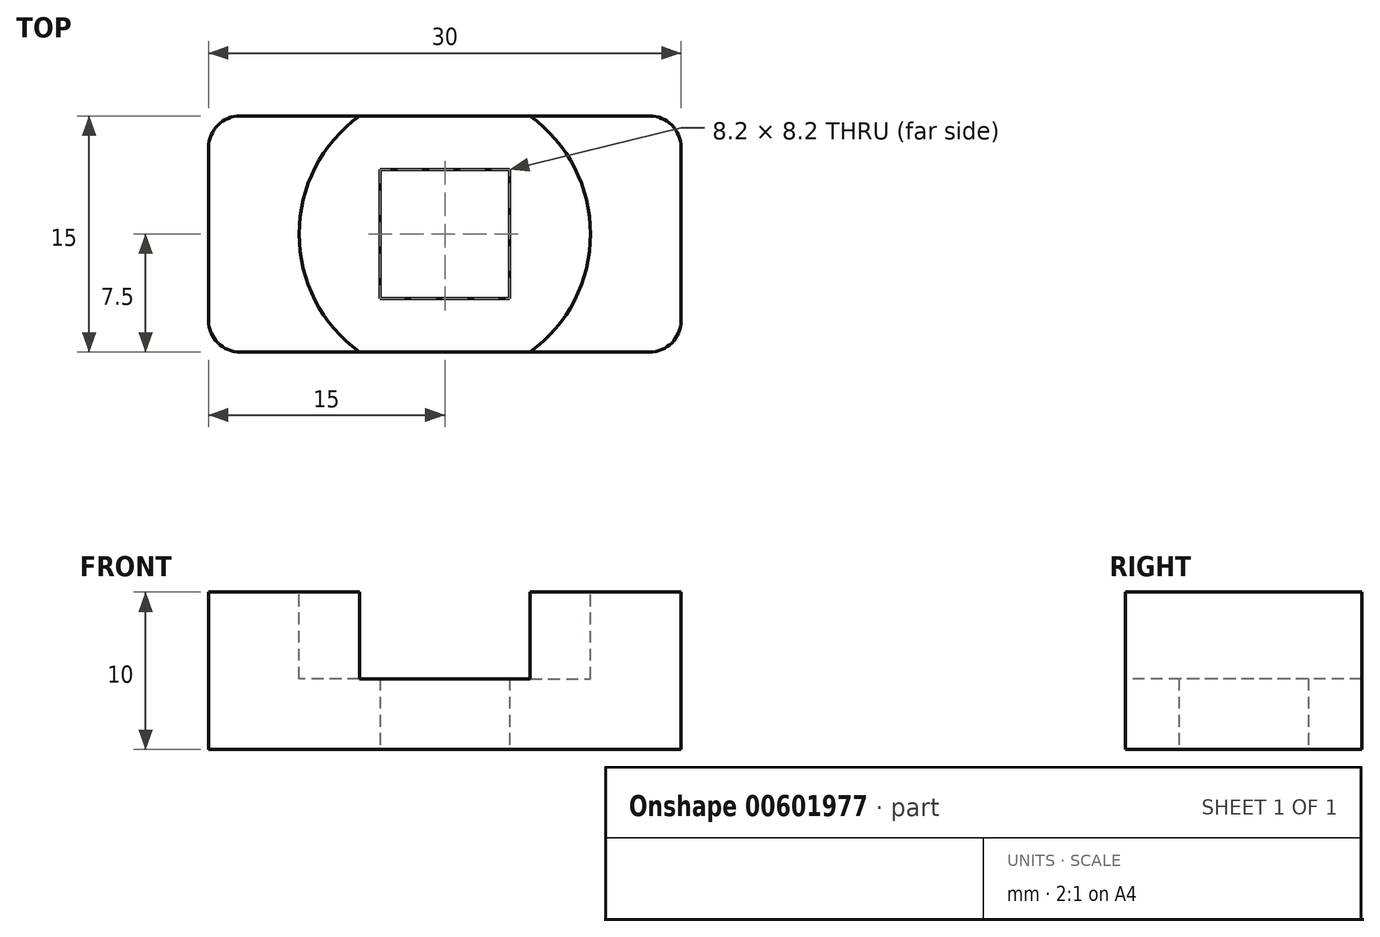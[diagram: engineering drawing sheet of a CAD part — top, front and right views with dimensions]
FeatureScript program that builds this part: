
annotation { "Feature Type Name" : "Feature", "Feature Type Description" : "" }
export const myFeature = defineFeature(function(context is Context, id is Id, definition is map)
    precondition{}
    {
        {
            var Q0;
            Q0=qCreatedBy(makeId("Top.planeOp"),FACE);
            var sketch = newSketch(context, id + "F0", { "sketchPlane" : qUnion([Q0])});
            skLineSegment(sketch, "E0.bottom", {"start": v(4.1, 4.1) * mm, "end": v(-4.1, 4.1) * mm});
            skLineSegment(sketch, "E0.top", {"start": v(4.1, -4.1) * mm, "end": v(-4.1, -4.1) * mm});
            skLineSegment(sketch, "E0.left", {"start": v(4.1, 4.1) * mm, "end": v(4.1, -4.1) * mm});
            skLineSegment(sketch, "E0.right", {"start": v(-4.1, 4.1) * mm, "end": v(-4.1, -4.1) * mm});
            skPoint(sketch, "E0.middle", {"position": v(0, 0) * mm});
            skLineSegment(sketch, "E1.bottom", {"start": v(13, 7.5) * mm, "end": v(-13, 7.5) * mm});
            skLineSegment(sketch, "E1.top", {"start": v(13, -7.5) * mm, "end": v(-13, -7.5) * mm});
            skLineSegment(sketch, "E1.left", {"start": v(15, 5.5) * mm, "end": v(15, -5.5) * mm});
            skLineSegment(sketch, "E1.right", {"start": v(-15, 5.5) * mm, "end": v(-15, -5.5) * mm});
            skPoint(sketch, "E2.visualSharp", {"position": v(15, 7.5) * mm});
            skArc(sketch, "E2.filletArc", {"start": v(15, 5.5) * mm, "mid": v(14.41, 6.91) * mm, "end": v(13, 7.5) * mm});
            skPoint(sketch, "E3.visualSharp", {"position": v(-15, 7.5) * mm});
            skArc(sketch, "E3.filletArc", {"start": v(-13, 7.5) * mm, "mid": v(-14.41, 6.91) * mm, "end": v(-15, 5.5) * mm});
            skPoint(sketch, "E4.visualSharp", {"position": v(-15, -7.5) * mm});
            skArc(sketch, "E4.filletArc", {"start": v(-15, -5.5) * mm, "mid": v(-14.41, -6.91) * mm, "end": v(-13, -7.5) * mm});
            skPoint(sketch, "E5.visualSharp", {"position": v(15, -7.5) * mm});
            skArc(sketch, "E5.filletArc", {"start": v(13, -7.5) * mm, "mid": v(14.41, -6.91) * mm, "end": v(15, -5.5) * mm});
            skSolve(sketch);
        }
        {
            var Q0;
            Q0=makeQuery(id+"F0.imprint","IMPRINT",FACE,{"disambiguationData":[TD([[makeQuery(id+"F0.imprint","IMPRINT",EDGE,{"derivedFrom":sQuery(id+"F0.wireOp",EDGE,"E0.bottom")}),-1.0]])]});
            extrude(context, id + "F1", {"entities" : qUnion([Q0]), "depth" : 10 * mm, "offsetDistance" : 25.4 * mm});
        }
        {
            var Q0;
            Q0=makeQuery(id+"F1.opExtrude","CAP_FACE",FACE,{"disambiguationData":[OSD([sQuery(id+"F0.wireOp",EDGE,"E0.bottom"),sQuery(id+"F0.wireOp",EDGE,"E0.top"),sQuery(id+"F0.wireOp",EDGE,"E0.left"),sQuery(id+"F0.wireOp",EDGE,"E0.right"),sQuery(id+"F0.wireOp",EDGE,"E1.bottom"),sQuery(id+"F0.wireOp",EDGE,"E1.top"),sQuery(id+"F0.wireOp",EDGE,"E1.left"),sQuery(id+"F0.wireOp",EDGE,"E1.right"),sQuery(id+"F0.wireOp",EDGE,"E2.filletArc"),sQuery(id+"F0.wireOp",EDGE,"E3.filletArc"),sQuery(id+"F0.wireOp",EDGE,"E4.filletArc"),sQuery(id+"F0.wireOp",EDGE,"E5.filletArc")])],"isStart":false});
            var sketch = newSketch(context, id + "F2", { "sketchPlane" : qUnion([Q0])});
            skCircle(sketch, "E6", {"center": v(0, 0) * mm, "radius": 9.25 * mm});
            skSolve(sketch);
        }
        {
            var Q0;
            Q0 = qSketchRegion(id + "F2", true);
            extrude(context, id + "F3", {"entities" : qUnion([Q0]), "operationType" : NewBodyOperationType.REMOVE, "oppositeDirection" : true, "depth" : 5.5 * mm, "offsetDistance" : 25.4 * mm});
        }
    });
